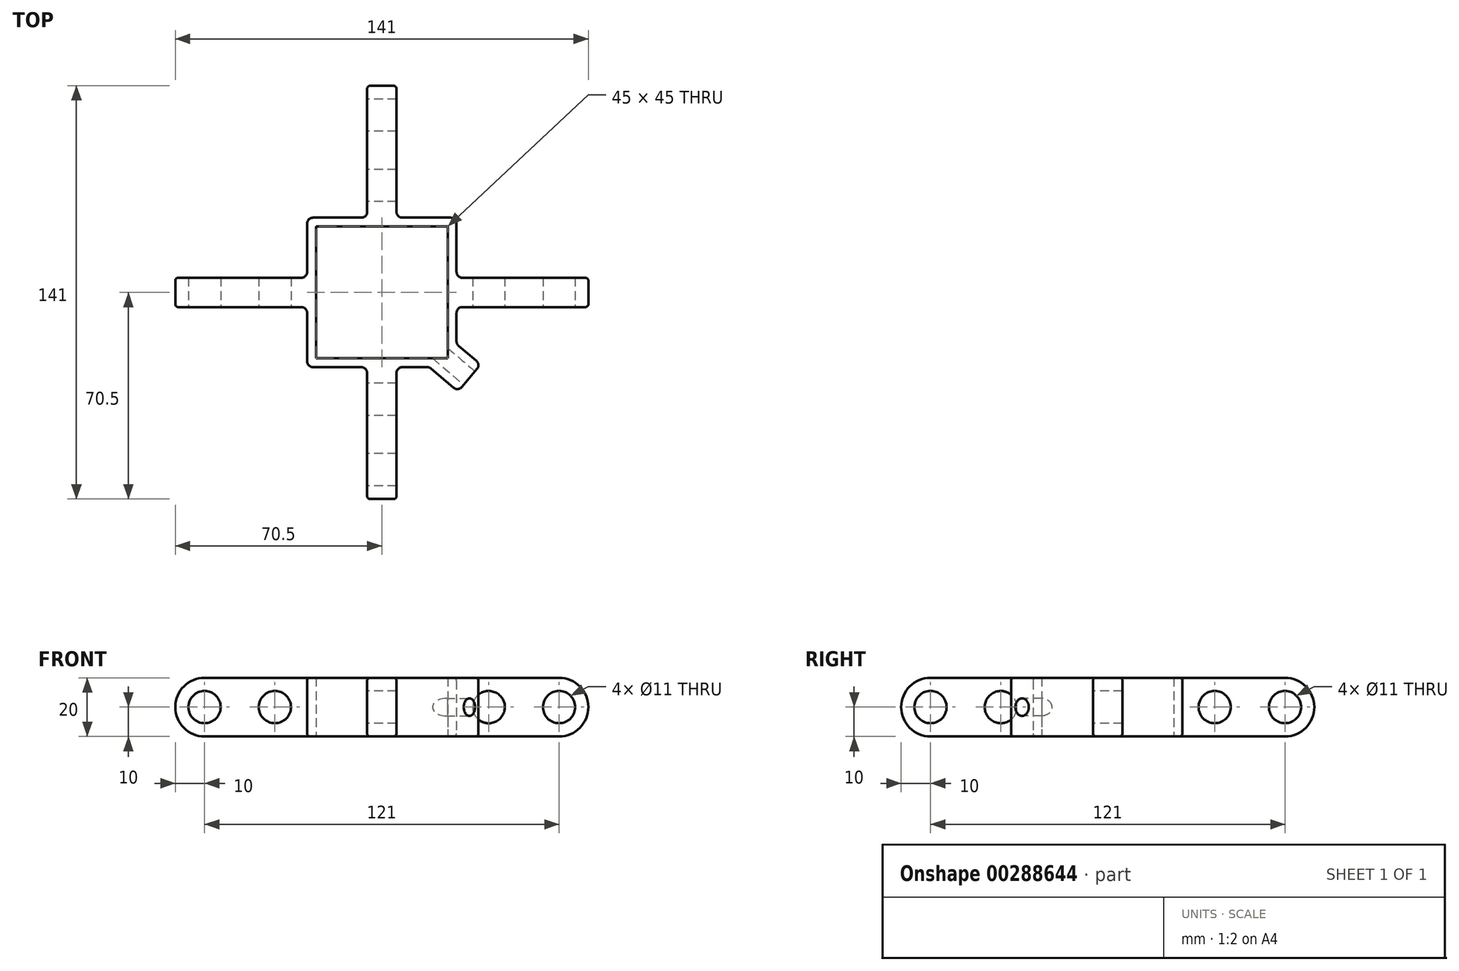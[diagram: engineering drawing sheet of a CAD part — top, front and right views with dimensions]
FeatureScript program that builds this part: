
annotation { "Feature Type Name" : "Feature", "Feature Type Description" : "" }
export const myFeature = defineFeature(function(context is Context, id is Id, definition is map)
    precondition{}
    {
        {
            var Q0;
            Q0=qCreatedBy(makeId("Top.planeOp"),FACE);
            var sketch = newSketch(context, id + "F0", { "sketchPlane" : qUnion([Q0])});
            skPoint(sketch, "E0.middle", {"position": v(0, 0) * mm});
            skLineSegment(sketch, "E1.bottom", {"start": v(-5, 25.5) * mm, "end": v(5, 25.5) * mm});
            skLineSegment(sketch, "E1.top", {"start": v(-5, 70.5) * mm, "end": v(5, 70.5) * mm});
            skLineSegment(sketch, "E1.left", {"start": v(-5, 25.5) * mm, "end": v(-5, 70.5) * mm});
            skLineSegment(sketch, "E1.right", {"start": v(5, 25.5) * mm, "end": v(5, 70.5) * mm});
            skLineSegment(sketch, "E2.bottom", {"start": v(25.5, 5) * mm, "end": v(70.5, 5) * mm});
            skLineSegment(sketch, "E2.top", {"start": v(25.5, -5) * mm, "end": v(70.5, -5) * mm});
            skLineSegment(sketch, "E2.left", {"start": v(25.5, 5) * mm, "end": v(25.5, -5) * mm});
            skLineSegment(sketch, "E2.right", {"start": v(70.5, 5) * mm, "end": v(70.5, -5) * mm});
            skLineSegment(sketch, "E3.bottom", {"start": v(5, -25.5) * mm, "end": v(-5, -25.5) * mm});
            skLineSegment(sketch, "E3.top", {"start": v(5, -70.5) * mm, "end": v(-5, -70.5) * mm});
            skLineSegment(sketch, "E3.left", {"start": v(5, -25.5) * mm, "end": v(5, -70.5) * mm});
            skLineSegment(sketch, "E3.right", {"start": v(-5, -25.5) * mm, "end": v(-5, -70.5) * mm});
            skLineSegment(sketch, "E4.bottom", {"start": v(-25.5, -5) * mm, "end": v(-70.5, -5) * mm});
            skLineSegment(sketch, "E4.top", {"start": v(-25.5, 5) * mm, "end": v(-70.5, 5) * mm});
            skLineSegment(sketch, "E4.left", {"start": v(-25.5, -5) * mm, "end": v(-25.5, 5) * mm});
            skLineSegment(sketch, "E4.right", {"start": v(-70.5, -5) * mm, "end": v(-70.5, 5) * mm});
            skLineSegment(sketch, "E5.bottom", {"start": v(22.5, 22.5) * mm, "end": v(-22.5, 22.5) * mm});
            skLineSegment(sketch, "E5.top", {"start": v(22.5, -22.5) * mm, "end": v(-22.5, -22.5) * mm});
            skLineSegment(sketch, "E5.left", {"start": v(22.5, 22.5) * mm, "end": v(22.5, -22.5) * mm});
            skLineSegment(sketch, "E5.right", {"start": v(-22.5, 22.5) * mm, "end": v(-22.5, -22.5) * mm});
            skLineSegment(sketch, "E6.bottom", {"start": v(25.5, 25.5) * mm, "end": v(-25.5, 25.5) * mm});
            skLineSegment(sketch, "E6.top", {"start": v(25.5, -25.5) * mm, "end": v(-25.5, -25.5) * mm});
            skLineSegment(sketch, "E6.left", {"start": v(25.5, 25.5) * mm, "end": v(25.5, -25.5) * mm});
            skLineSegment(sketch, "E6.right", {"start": v(-25.5, 25.5) * mm, "end": v(-25.5, -25.5) * mm});
            skLineSegment(sketch, "E7", {"start": v(25.5, -17.62) * mm, "end": v(33.78, -24.67) * mm});
            skLineSegment(sketch, "E8", {"start": v(33.78, -24.67) * mm, "end": v(26, -33.8) * mm});
            skLineSegment(sketch, "E9", {"start": v(26, -33.8) * mm, "end": v(16.24, -25.5) * mm});
            skSolve(sketch);
        }
        {
            var Q0;
            Q0=makeQuery(id+"F0.imprint","IMPRINT",FACE,{"disambiguationData":[TD([[makeQuery(id+"F0.imprint","IMPRINT",EDGE,{"derivedFrom":sQuery(id+"F0.wireOp",EDGE,"E1.top")}),-1.0]])]});
            var Q1;
            {var subQ0=sQuery(id+"F0.wireOp",EDGE,"E4.bottom");Q1=makeQuery(id+"F0.imprint","IMPRINT",FACE,{"disambiguationData":[TD([[makeQuery(id+"F0.imprint","IMPRINT",EDGE,{"derivedFrom":subQ0}),-1.0]])]});}
            var Q2;
            Q2=makeQuery(id+"F0.imprint","IMPRINT",FACE,{"disambiguationData":[TD([[makeQuery(id+"F0.imprint","IMPRINT",EDGE,{"derivedFrom":sQuery(id+"F0.wireOp",EDGE,"E3.top")}),-1.0]])]});
            var Q3;
            {var subQ0=sQuery(id+"F0.wireOp",EDGE,"E2.bottom");Q3=makeQuery(id+"F0.imprint","IMPRINT",FACE,{"disambiguationData":[TD([[makeQuery(id+"F0.imprint","IMPRINT",EDGE,{"derivedFrom":subQ0}),-1.0]])]});}
            var Q4;
            Q4=makeQuery(id+"F0.imprint","IMPRINT",FACE,{"disambiguationData":[TD([[makeQuery(id+"F0.imprint","IMPRINT",EDGE,{"derivedFrom":sQuery(id+"F0.wireOp",EDGE,"E5.bottom")}),-1.0]])]});
            var Q5;
            {var subQ0=sQuery(id+"F0.wireOp",EDGE,"E7");Q5=makeQuery(id+"F0.imprint","IMPRINT",FACE,{"disambiguationData":[TD([[makeQuery(id+"F0.imprint","IMPRINT",EDGE,{"derivedFrom":subQ0}),-1.0]])]});}
            extrude(context, id + "F1", {"entities" : qUnion([Q0, Q1, Q2, Q3, Q4, Q5]), "depth" : 20 * mm});
        }
        {
            var Q0;
            Q0=makeQuery(id+"F1.opExtrude","SWEPT_FACE",FACE,{"disambiguationData":[OSD([sQuery(id+"F0.wireOp",EDGE,"E2.top")])]});
            var sketch = newSketch(context, id + "F2", { "sketchPlane" : qUnion([Q0])});
            skCircle(sketch, "E10", {"center": v(60.5, 10) * mm, "radius": 5.5 * mm});
            skCircle(sketch, "E11", {"center": v(36.5, 10) * mm, "radius": 5.5 * mm});
            skCircle(sketch, "E12", {"center": v(-60.5, 10) * mm, "radius": 5.5 * mm});
            skCircle(sketch, "E13", {"center": v(-36.5, 10) * mm, "radius": 5.5 * mm});
            skSolve(sketch);
        }
        {
            var Q0;
            Q0=makeQuery(id+"F2.imprint","IMPRINT",FACE,{"disambiguationData":[TD([[makeQuery(id+"F2.imprint","IMPRINT",EDGE,{"derivedFrom":sQuery(id+"F2.wireOp",EDGE,"E11")}),1.0]])]});
            var Q1;
            Q1=makeQuery(id+"F2.imprint","IMPRINT",FACE,{"disambiguationData":[TD([[makeQuery(id+"F2.imprint","IMPRINT",EDGE,{"derivedFrom":sQuery(id+"F2.wireOp",EDGE,"E10")}),1.0]])]});
            var Q2;
            Q2=makeQuery(id+"F2.imprint","IMPRINT",FACE,{"disambiguationData":[TD([[makeQuery(id+"F2.imprint","IMPRINT",EDGE,{"derivedFrom":sQuery(id+"F2.wireOp",EDGE,"E13")}),1.0]])]});
            var Q3;
            Q3=makeQuery(id+"F2.imprint","IMPRINT",FACE,{"disambiguationData":[TD([[makeQuery(id+"F2.imprint","IMPRINT",EDGE,{"derivedFrom":sQuery(id+"F2.wireOp",EDGE,"E12")}),1.0]])]});
            extrude(context, id + "F3", {"entities" : qUnion([Q0, Q1, Q2, Q3]), "operationType" : NewBodyOperationType.REMOVE, "oppositeDirection" : true, "depth" : 10 * mm, "offsetDistance" : 25 * mm});
        }
        {
            var Q0;
            Q0=makeQuery(id+"F1.opExtrude","SWEPT_FACE",FACE,{"disambiguationData":[OSD([sQuery(id+"F0.wireOp",EDGE,"E3.right")])]});
            var sketch = newSketch(context, id + "F4", { "sketchPlane" : qUnion([Q0])});
            skCircle(sketch, "E14", {"center": v(60.5, 10) * mm, "radius": 5.5 * mm});
            skCircle(sketch, "E15", {"center": v(36.5, 10) * mm, "radius": 5.5 * mm});
            skCircle(sketch, "E16", {"center": v(-60.5, 10) * mm, "radius": 5.5 * mm});
            skCircle(sketch, "E17", {"center": v(-36.5, 10) * mm, "radius": 5.5 * mm});
            skSolve(sketch);
        }
        {
            var Q0;
            Q0=makeQuery(id+"F4.imprint","IMPRINT",FACE,{"disambiguationData":[TD([[makeQuery(id+"F4.imprint","IMPRINT",EDGE,{"derivedFrom":sQuery(id+"F4.wireOp",EDGE,"E15")}),1.0]])]});
            var Q1;
            Q1=makeQuery(id+"F4.imprint","IMPRINT",FACE,{"disambiguationData":[TD([[makeQuery(id+"F4.imprint","IMPRINT",EDGE,{"derivedFrom":sQuery(id+"F4.wireOp",EDGE,"E14")}),1.0]])]});
            var Q2;
            Q2=makeQuery(id+"F4.imprint","IMPRINT",FACE,{"disambiguationData":[TD([[makeQuery(id+"F4.imprint","IMPRINT",EDGE,{"derivedFrom":sQuery(id+"F4.wireOp",EDGE,"E17")}),1.0]])]});
            var Q3;
            Q3=makeQuery(id+"F4.imprint","IMPRINT",FACE,{"disambiguationData":[TD([[makeQuery(id+"F4.imprint","IMPRINT",EDGE,{"derivedFrom":sQuery(id+"F4.wireOp",EDGE,"E16")}),1.0]])]});
            extrude(context, id + "F5", {"entities" : qUnion([Q0, Q1, Q2, Q3]), "operationType" : NewBodyOperationType.REMOVE, "oppositeDirection" : true, "depth" : 10 * mm, "offsetDistance" : 25 * mm});
        }
        {
            var Q0;
            Q0=makeQuery(id+"F1.opExtrude","CAP_EDGE",EDGE,{"disambiguationData":[OSD([sQuery(id+"F0.wireOp",EDGE,"E1.top")])],"isStart":false});
            var Q1;
            Q1=makeQuery(id+"F1.opExtrude","CAP_EDGE",EDGE,{"disambiguationData":[OSD([sQuery(id+"F0.wireOp",EDGE,"E1.top")])],"isStart":true});
            var Q2;
            Q2=makeQuery(id+"F1.opExtrude","CAP_EDGE",EDGE,{"disambiguationData":[OSD([sQuery(id+"F0.wireOp",EDGE,"E4.right")])],"isStart":true});
            var Q3;
            Q3=makeQuery(id+"F1.opExtrude","CAP_EDGE",EDGE,{"disambiguationData":[OSD([sQuery(id+"F0.wireOp",EDGE,"E3.top")])],"isStart":false});
            var Q4;
            Q4=makeQuery(id+"F1.opExtrude","CAP_EDGE",EDGE,{"disambiguationData":[OSD([sQuery(id+"F0.wireOp",EDGE,"E2.right")])],"isStart":false});
            var Q5;
            Q5=makeQuery(id+"F1.opExtrude","CAP_EDGE",EDGE,{"disambiguationData":[OSD([sQuery(id+"F0.wireOp",EDGE,"E4.right")])],"isStart":false});
            var Q6;
            Q6=makeQuery(id+"F1.opExtrude","CAP_EDGE",EDGE,{"disambiguationData":[OSD([sQuery(id+"F0.wireOp",EDGE,"E3.top")])],"isStart":true});
            var Q7;
            Q7=makeQuery(id+"F1.opExtrude","CAP_EDGE",EDGE,{"disambiguationData":[OSD([sQuery(id+"F0.wireOp",EDGE,"E2.right")])],"isStart":true});
            fillet(context, id + "F6", {"entities" : qUnion([Q0, Q1, Q2, Q3, Q4, Q5, Q6, Q7]), "radius" : 10 * mm, "tangentPropagation" : true, "allowEdgeOverflow" : false});
        }
        {
            var Q0;
            Q0=makeQuery(id+"F1.opExtrude","SWEPT_FACE",FACE,{"disambiguationData":[OSD([sQuery(id+"F0.wireOp",EDGE,"E8")])]});
            var sketch = newSketch(context, id + "F7", { "sketchPlane" : qUnion([Q0])});
            skCircle(sketch, "E18", {"center": v(-2.9, 10) * mm, "radius": 3 * mm});
            skSolve(sketch);
        }
        {
            var Q0;
            Q0=makeQuery(id+"F7.imprint","IMPRINT",FACE,{"disambiguationData":[TD([[makeQuery(id+"F7.imprint","IMPRINT",EDGE,{"derivedFrom":sQuery(id+"F7.wireOp",EDGE,"E18")}),1.0]])]});
            var Q1;
            Q1=sQuery(id+"F7.wireOp",EDGE,"E18");
            extrude(context, id + "F8", {"entities" : qUnion([Q0]), "operationType" : NewBodyOperationType.REMOVE, "surfaceEntities" : qUnion([Q1]), "oppositeDirection" : true, "depth" : 25 * mm});
        }
        {
            var Q0;
            Q0=makeQuery(id+"F1.opExtrude","SWEPT_EDGE",EDGE,{"disambiguationData":[OSD([sQuery(id+"F0.wireOp",EDGE,"E4.bottom"),sQuery(id+"F0.wireOp",EDGE,"E6.right")])]});
            var Q1;
            Q1=makeQuery(id+"F1.opExtrude","SWEPT_EDGE",EDGE,{"disambiguationData":[OSD([sQuery(id+"F0.wireOp",EDGE,"E3.right"),sQuery(id+"F0.wireOp",EDGE,"E6.top")])]});
            var Q2;
            Q2=makeQuery(id+"F1.opExtrude","SWEPT_EDGE",EDGE,{"disambiguationData":[OSD([sQuery(id+"F0.wireOp",EDGE,"E6.top"),sQuery(id+"F0.wireOp",EDGE,"E9")])]});
            var Q3;
            Q3=makeQuery(id+"F1.opExtrude","SWEPT_EDGE",EDGE,{"disambiguationData":[OSD([sQuery(id+"F0.wireOp",EDGE,"E3.left"),sQuery(id+"F0.wireOp",EDGE,"E6.top")])]});
            var Q4;
            Q4=makeQuery(id+"F1.opExtrude","SWEPT_EDGE",EDGE,{"disambiguationData":[OSD([sQuery(id+"F0.wireOp",EDGE,"E1.left"),sQuery(id+"F0.wireOp",EDGE,"E6.bottom")])]});
            var Q5;
            Q5=makeQuery(id+"F1.opExtrude","SWEPT_EDGE",EDGE,{"disambiguationData":[OSD([sQuery(id+"F0.wireOp",EDGE,"E4.top"),sQuery(id+"F0.wireOp",EDGE,"E6.right")])]});
            var Q6;
            Q6=makeQuery(id+"F1.opExtrude","SWEPT_EDGE",EDGE,{"disambiguationData":[OSD([sQuery(id+"F0.wireOp",EDGE,"E1.right"),sQuery(id+"F0.wireOp",EDGE,"E6.bottom")])]});
            var Q7;
            Q7=makeQuery(id+"F1.opExtrude","SWEPT_EDGE",EDGE,{"disambiguationData":[OSD([sQuery(id+"F0.wireOp",EDGE,"E2.bottom"),sQuery(id+"F0.wireOp",EDGE,"E6.left")])]});
            var Q8;
            Q8=makeQuery(id+"F1.opExtrude","SWEPT_EDGE",EDGE,{"disambiguationData":[OSD([sQuery(id+"F0.wireOp",EDGE,"E6.left"),sQuery(id+"F0.wireOp",EDGE,"E7")])]});
            var Q9;
            Q9=makeQuery(id+"F1.opExtrude","SWEPT_EDGE",EDGE,{"disambiguationData":[OSD([sQuery(id+"F0.wireOp",EDGE,"E2.top"),sQuery(id+"F0.wireOp",EDGE,"E6.left")])]});
            var Q10;
            Q10=makeQuery(id+"F1.opExtrude","SWEPT_EDGE",EDGE,{"disambiguationData":[OSD([sQuery(id+"F0.wireOp",EDGE,"E6.top"),sQuery(id+"F0.wireOp",EDGE,"E6.right")])]});
            var Q11;
            Q11=makeQuery(id+"F1.opExtrude","SWEPT_EDGE",EDGE,{"disambiguationData":[OSD([sQuery(id+"F0.wireOp",EDGE,"E6.bottom"),sQuery(id+"F0.wireOp",EDGE,"E6.left")])]});
            var Q12;
            Q12=makeQuery(id+"F1.opExtrude","SWEPT_EDGE",EDGE,{"disambiguationData":[OSD([sQuery(id+"F0.wireOp",EDGE,"E6.bottom"),sQuery(id+"F0.wireOp",EDGE,"E6.right")])]});
            var Q13;
            Q13=makeQuery(id+"F1.opExtrude","SWEPT_EDGE",EDGE,{"disambiguationData":[OSD([sQuery(id+"F0.wireOp",EDGE,"E8"),sQuery(id+"F0.wireOp",EDGE,"E9")])]});
            var Q14;
            Q14=makeQuery(id+"F1.opExtrude","SWEPT_EDGE",EDGE,{"disambiguationData":[OSD([sQuery(id+"F0.wireOp",EDGE,"E7"),sQuery(id+"F0.wireOp",EDGE,"E8")])]});
            fillet(context, id + "F9", {"entities" : qUnion([Q0, Q1, Q2, Q3, Q4, Q5, Q6, Q7, Q8, Q9, Q10, Q11, Q12, Q13, Q14]), "radius" : 2 * mm, "tangentPropagation" : true, "allowEdgeOverflow" : false});
        }
        {
            var Q0;
            {var subQ0=sQuery(id+"F0.wireOp",EDGE,"E6.bottom");Q0=makeQuery(id+"F1.opExtrude","CAP_EDGE",EDGE,{"disambiguationData":[OSD([subQ0]),TDD([makeQuery(id+"F0.imprint","IMPRINT",EDGE,{"disambiguationData":[TD([[makeQuery(id+"F0.imprint","INTERSECT",VERTEX,{"derivedFrom":[sQuery(id+"F0.wireOp",EDGE,"E1.left"),subQ0]}),-1.0]])],"derivedFrom":subQ0})])],"isStart":false});}
            var Q1;
            {var subQ0=sQuery(id+"F0.wireOp",EDGE,"E6.right");Q1=makeQuery(id+"F1.opExtrude","CAP_EDGE",EDGE,{"disambiguationData":[OSD([subQ0]),TDD([makeQuery(id+"F0.imprint","IMPRINT",EDGE,{"disambiguationData":[TD([[makeQuery(id+"F0.imprint","INTERSECT",VERTEX,{"derivedFrom":[sQuery(id+"F0.wireOp",EDGE,"E4.top"),subQ0]}),1.0]])],"derivedFrom":subQ0})])],"isStart":false});}
            var Q2;
            {var subQ0=sQuery(id+"F0.wireOp",EDGE,"E6.right");Q2=makeQuery(id+"F1.opExtrude","CAP_EDGE",EDGE,{"disambiguationData":[OSD([subQ0]),TDD([makeQuery(id+"F0.imprint","IMPRINT",EDGE,{"disambiguationData":[TD([[makeQuery(id+"F0.imprint","INTERSECT",VERTEX,{"derivedFrom":[sQuery(id+"F0.wireOp",EDGE,"E4.bottom"),subQ0]}),-1.0]])],"derivedFrom":subQ0})])],"isStart":false});}
            var Q3;
            {var subQ0=sQuery(id+"F0.wireOp",EDGE,"E6.top");Q3=makeQuery(id+"F1.opExtrude","CAP_EDGE",EDGE,{"disambiguationData":[OSD([subQ0]),TDD([makeQuery(id+"F0.imprint","IMPRINT",EDGE,{"disambiguationData":[TD([[makeQuery(id+"F0.imprint","INTERSECT",VERTEX,{"derivedFrom":[sQuery(id+"F0.wireOp",EDGE,"E3.right"),subQ0]}),-1.0]])],"derivedFrom":subQ0})])],"isStart":false});}
            var Q4;
            {var subQ0=sQuery(id+"F0.wireOp",EDGE,"E6.top");Q4=makeQuery(id+"F1.opExtrude","CAP_EDGE",EDGE,{"disambiguationData":[OSD([subQ0]),TDD([makeQuery(id+"F0.imprint","IMPRINT",EDGE,{"disambiguationData":[TD([[makeQuery(id+"F0.imprint","INTERSECT",VERTEX,{"derivedFrom":[sQuery(id+"F0.wireOp",EDGE,"E3.left"),subQ0]}),1.0]])],"derivedFrom":subQ0})])],"isStart":false});}
            var Q5;
            Q5=makeQuery(id+"F1.opExtrude","CAP_EDGE",EDGE,{"disambiguationData":[OSD([sQuery(id+"F0.wireOp",EDGE,"E8")])],"isStart":false});
            var Q6;
            {var subQ0=sQuery(id+"F0.wireOp",EDGE,"E6.left");Q6=makeQuery(id+"F1.opExtrude","CAP_EDGE",EDGE,{"disambiguationData":[OSD([subQ0]),TDD([makeQuery(id+"F0.imprint","IMPRINT",EDGE,{"disambiguationData":[TD([[makeQuery(id+"F0.imprint","INTERSECT",VERTEX,{"derivedFrom":[sQuery(id+"F0.wireOp",EDGE,"E2.top"),subQ0]}),-1.0]])],"derivedFrom":subQ0})])],"isStart":false});}
            var Q7;
            {var subQ0=sQuery(id+"F0.wireOp",EDGE,"E6.left");Q7=makeQuery(id+"F1.opExtrude","CAP_EDGE",EDGE,{"disambiguationData":[OSD([subQ0]),TDD([makeQuery(id+"F0.imprint","IMPRINT",EDGE,{"disambiguationData":[TD([[makeQuery(id+"F0.imprint","INTERSECT",VERTEX,{"derivedFrom":[sQuery(id+"F0.wireOp",EDGE,"E2.bottom"),subQ0]}),1.0]])],"derivedFrom":subQ0})])],"isStart":false});}
            var Q8;
            {var subQ0=sQuery(id+"F0.wireOp",EDGE,"E6.bottom");Q8=makeQuery(id+"F1.opExtrude","CAP_EDGE",EDGE,{"disambiguationData":[OSD([subQ0]),TDD([makeQuery(id+"F0.imprint","IMPRINT",EDGE,{"disambiguationData":[TD([[makeQuery(id+"F0.imprint","INTERSECT",VERTEX,{"derivedFrom":[sQuery(id+"F0.wireOp",EDGE,"E1.right"),subQ0]}),1.0]])],"derivedFrom":subQ0})])],"isStart":false});}
            var Q9;
            Q9=makeQuery(id+"F1.opExtrude","SWEPT_EDGE",EDGE,{"disambiguationData":[OSD([sQuery(id+"F0.wireOp",EDGE,"E8"),sQuery(id+"F0.wireOp",EDGE,"E9")])]});
            var Q10;
            Q10=makeQuery(id+"F1.opExtrude","SWEPT_EDGE",EDGE,{"disambiguationData":[OSD([sQuery(id+"F0.wireOp",EDGE,"E7"),sQuery(id+"F0.wireOp",EDGE,"E8")])]});
            fillet(context, id + "F10", {"entities" : qUnion([Q0, Q1, Q2, Q3, Q4, Q5, Q6, Q7, Q8, Q9, Q10]), "radius" : 1 * mm, "tangentPropagation" : true, "allowEdgeOverflow" : false});
        }
    });
